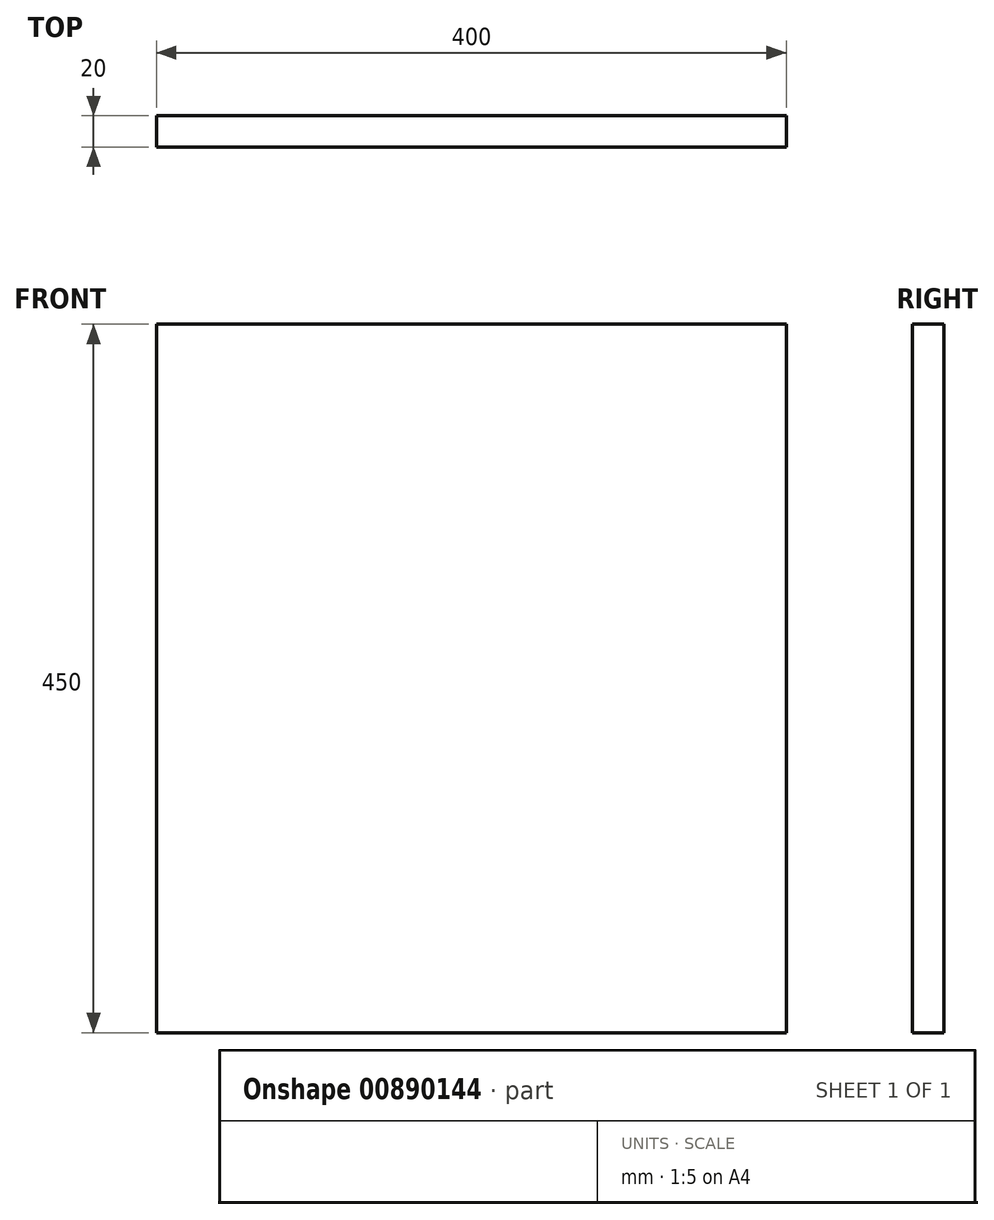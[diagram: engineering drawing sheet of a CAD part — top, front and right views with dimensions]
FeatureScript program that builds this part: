
annotation { "Feature Type Name" : "Feature", "Feature Type Description" : "" }
export const myFeature = defineFeature(function(context is Context, id is Id, definition is map)
    precondition{}
    {
        {
            var Q0;
            Q0=qCreatedBy(makeId("Front.planeOp"),FACE);
            var sketch = newSketch(context, id + "F0", { "sketchPlane" : qUnion([Q0])});
            skLineSegment(sketch, "E0.bottom", {"start": v(-200, 225) * mm, "end": v(200, 225) * mm});
            skLineSegment(sketch, "E0.top", {"start": v(-200, -225) * mm, "end": v(200, -225) * mm});
            skLineSegment(sketch, "E0.left", {"start": v(-200, 225) * mm, "end": v(-200, -225) * mm});
            skLineSegment(sketch, "E0.right", {"start": v(200, 225) * mm, "end": v(200, -225) * mm});
            skPoint(sketch, "E0.middle", {"position": v(0, 0) * mm});
            skSolve(sketch);
        }
        {
            var Q0;
            Q0=qSketchRegion(id+"F0",true);
            extrude(context, id + "F1", {"entities" : qUnion([Q0]), "depth" : 20 * mm, "offsetDistance" : 25 * mm});
        }
    });
